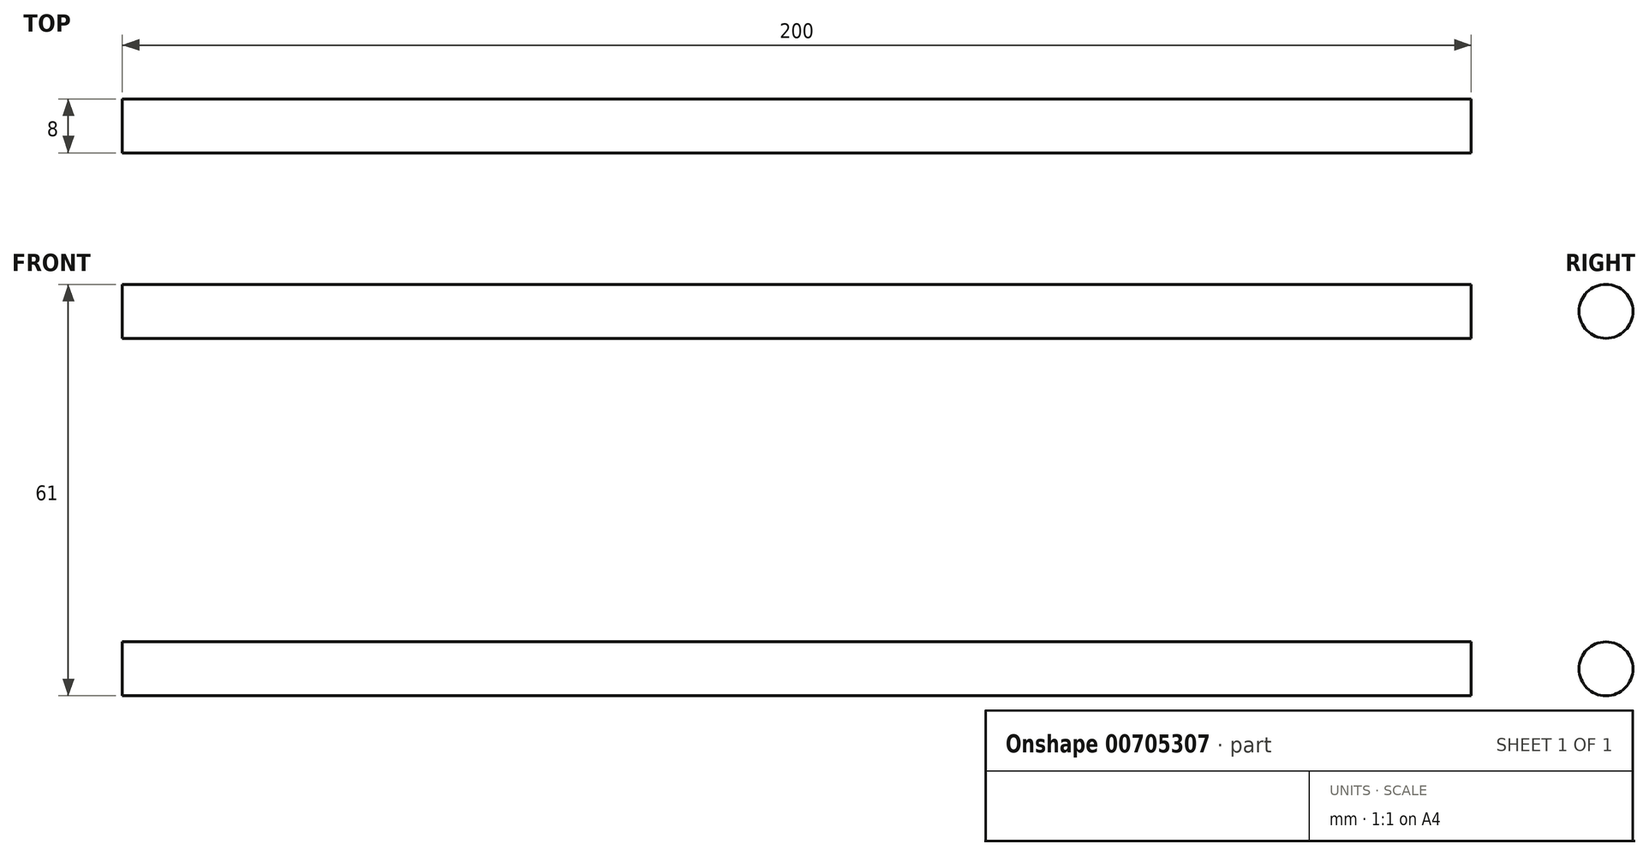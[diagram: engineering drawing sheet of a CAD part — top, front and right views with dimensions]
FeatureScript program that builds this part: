
annotation { "Feature Type Name" : "Feature", "Feature Type Description" : "" }
export const myFeature = defineFeature(function(context is Context, id is Id, definition is map)
    precondition{}
    {
        {
            var Q0;
            Q0=qCreatedBy(makeId("Right.planeOp"),FACE);
            var sketch = newSketch(context, id + "F0", { "sketchPlane" : qUnion([Q0])});
            skCircle(sketch, "E0", {"center": v(0, 26.5) * mm, "radius": 4 * mm});
            skCircle(sketch, "E1.MirrorC", {"center": v(0, -26.5) * mm, "radius": 4 * mm});
            skSolve(sketch);
        }
        {
            var Q0;
            Q0 = qSketchRegion(id + "F0", true);
            extrude(context, id + "F1", {"entities" : qUnion([Q0]), "endBound" : BoundingType.SYMMETRIC, "depth" : 200 * mm, "offsetDistance" : 25 * mm});
        }
    });
